# Revit family: Lighting-Wall Mount-Amerlux-Rook350-Round
name_source: partatom
category: Lighting Fixtures
units: mm (PartAtom-declared; Revit-internal decimal feet)

## family parameters
Cut with Voids When Loaded = No
Host = Face
Light Source = Yes
Part Type = Normal
Room Calculation Point = No
Round Connector Dimension = Use Diameter
Shared = No

## types (2) — shared parameters
Apparent Load = 0 VA
Back Plate Height = 5.17 "
Color Filter = 16777215
Default Elevation = 48 "
Description = Wall Mount
Dimming Lamp Color Temperature Shift = <None>
Emit Shape Visible in Rendering = No
Emit from Circle Diameter = 4 "
Fixture Finish = Aluminum Finish
Manufacturer = Amerlux
Model = Rook 350
Number of Poles = 1
Photometric Web File = Load File
Power Factor = 1
Tilt Angle = -90.00°
URL = http://www.amerlux.com
Voltage = 0 V

## per-type parameters (varying)
| type | Height |
| Wall Mount | 11.5 " |
| Remote | 6.5 " |

## geometry (parser evidence)
native form markers: Sweep x5
no freeform markers — native parametric forms only
